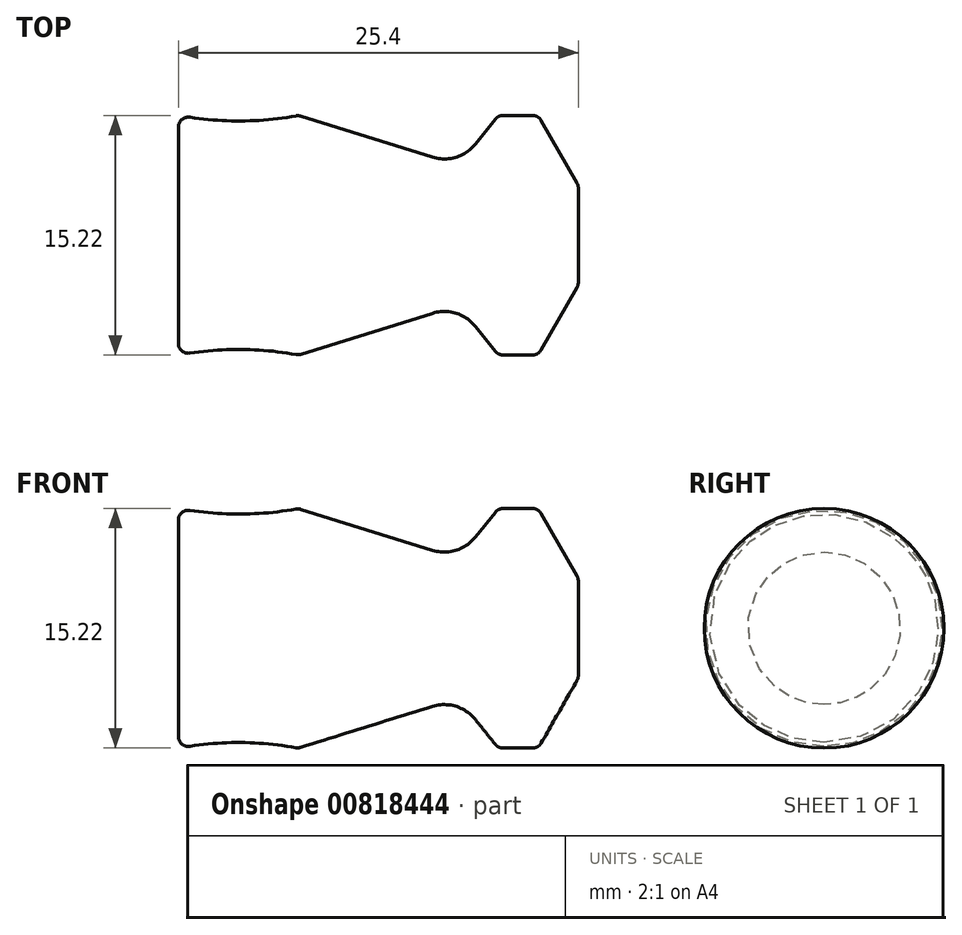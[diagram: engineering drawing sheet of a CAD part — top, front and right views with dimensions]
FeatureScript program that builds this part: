
annotation { "Feature Type Name" : "Feature", "Feature Type Description" : "" }
export const myFeature = defineFeature(function(context is Context, id is Id, definition is map)
    precondition{}
    {
        {
            var Q0;
            Q0=qCreatedBy(makeId("Top.planeOp"),FACE);
            var sketch = newSketch(context, id + "F0", { "sketchPlane" : qUnion([Q0])});
            skLineSegment(sketch, "E0", {"start": v(0, 0) * mm, "end": v(-25.4, 0) * mm});
            skLineSegment(sketch, "E1", {"start": v(-25.4, 0) * mm, "end": v(-25.4, 6.87) * mm});
            skLineSegment(sketch, "E2", {"start": v(0, 0) * mm, "end": v(0, 3) * mm});
            skLineSegment(sketch, "E3", {"start": v(-0.08, 3.32) * mm, "end": v(-2.36, 7.3) * mm});
            skLineSegment(sketch, "E4", {"start": v(-2.9, 7.6) * mm, "end": v(-4.78, 7.6) * mm});
            skLineSegment(sketch, "E5", {"start": v(-5.27, 7.37) * mm, "end": v(-6.54, 5.8) * mm});
            skLineSegment(sketch, "E6", {"start": v(-17.63, 7.56) * mm, "end": v(-9.27, 4.96) * mm});
            skPoint(sketch, "E7.visualSharp", {"position": v(-25.4, 7.62) * mm});
            skPoint(sketch, "E8.visualSharp", {"position": v(-5.08, 7.6) * mm});
            skArc(sketch, "E8.filletArc", {"start": v(-4.78, 7.6) * mm, "mid": v(-5.05, 7.55) * mm, "end": v(-5.27, 7.37) * mm});
            skPoint(sketch, "E9.visualSharp", {"position": v(-2.54, 7.6) * mm});
            skArc(sketch, "E9.filletArc", {"start": v(-2.36, 7.3) * mm, "mid": v(-2.59, 7.52) * mm, "end": v(-2.9, 7.6) * mm});
            skPoint(sketch, "E10.visualSharp", {"position": v(0, 3.18) * mm});
            skArc(sketch, "E10.filletArc", {"start": v(0, 3) * mm, "mid": v(-0.02, 3.17) * mm, "end": v(-0.08, 3.32) * mm});
            skPoint(sketch, "E11.visualSharp", {"position": v(-17.78, 7.6) * mm});
            skPoint(sketch, "E12.visualSharp", {"position": v(-7.62, 4.44) * mm});
            skArc(sketch, "E12.filletArc", {"start": v(-9.27, 4.96) * mm, "mid": v(-7.78, 4.96) * mm, "end": v(-6.54, 5.8) * mm});
            skArc(sketch, "E13", {"start": v(-24.67, 7.5) * mm, "mid": v(-21.3, 7.26) * mm, "end": v(-17.93, 7.58) * mm});
            skArc(sketch, "E14.filletArc", {"start": v(-24.67, 7.5) * mm, "mid": v(-25.18, 7.35) * mm, "end": v(-25.4, 6.87) * mm});
            skArc(sketch, "E15.filletArc", {"start": v(-17.63, 7.56) * mm, "mid": v(-17.78, 7.6) * mm, "end": v(-17.93, 7.58) * mm});
            skSolve(sketch);
        }
        {
            var Q0;
            Q0=makeQuery(id+"F0.imprint","IMPRINT",FACE,{"disambiguationData":[TD([[makeQuery(id+"F0.imprint","IMPRINT",EDGE,{"derivedFrom":sQuery(id+"F0.wireOp",EDGE,"E0")}),-1.0]])]});
            var Q1;
            Q1=sQuery(id+"F0.wireOp",EDGE,"E0");
            revolve(context, id + "F1", {"surfaceOperationType" : NewSurfaceOperationType.NEW, "entities" : qUnion([Q0]), "axis" : qUnion([Q1]), "revolveType" : RevolveType.FULL});
        }
    });
